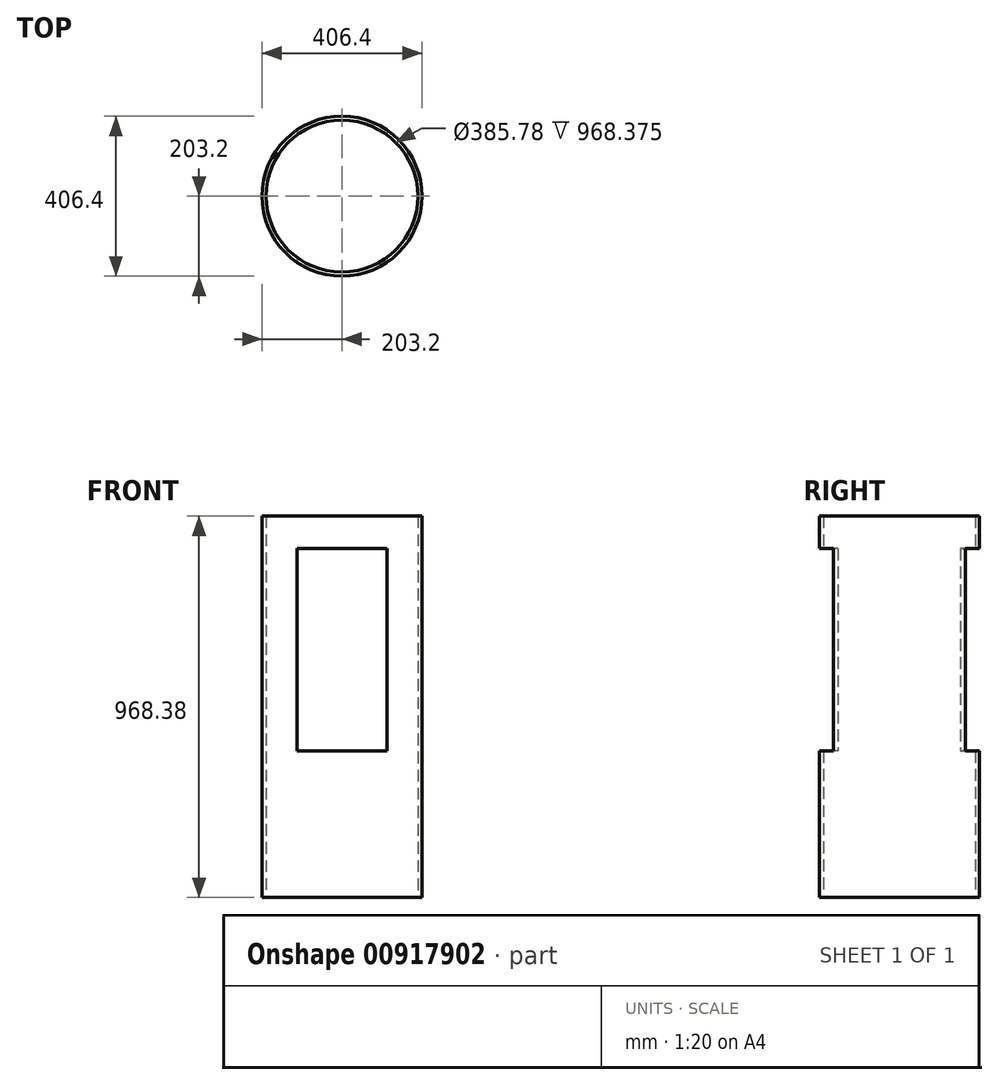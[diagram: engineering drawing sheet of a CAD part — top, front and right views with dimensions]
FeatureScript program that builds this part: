
annotation { "Feature Type Name" : "Feature", "Feature Type Description" : "" }
export const myFeature = defineFeature(function(context is Context, id is Id, definition is map)
    precondition{}
    {
        {
            var Q0;
            Q0=qCreatedBy(makeId("Top.planeOp"),FACE);
            var sketch = newSketch(context, id + "F0", { "sketchPlane" : qUnion([Q0])});
            skCircle(sketch, "E0", {"center": v(0, 0) * mm, "radius": 203.2 * mm});
            skCircle(sketch, "E1", {"center": v(0, 0) * mm, "radius": 192.89 * mm});
            skSolve(sketch);
        }
        {
            var Q0;
            Q0 = qSketchRegion(id + "F0", true);
            extrude(context, id + "F1", {"entities" : qUnion([Q0]), "depth" : 968.38 * mm, "offsetDistance" : 25.4 * mm});
        }
        {
            var Q0;
            Q0=qCreatedBy(makeId("Front.planeOp"),FACE);
            var sketch = newSketch(context, id + "F2", { "sketchPlane" : qUnion([Q0])});
            skLineSegment(sketch, "E2.bottom", {"start": v(114.3, 886.43) * mm, "end": v(-114.3, 886.43) * mm});
            skLineSegment(sketch, "E2.top", {"start": v(114.3, 372.13) * mm, "end": v(-114.3, 372.13) * mm});
            skLineSegment(sketch, "E2.left", {"start": v(114.3, 886.43) * mm, "end": v(114.3, 372.13) * mm});
            skLineSegment(sketch, "E2.right", {"start": v(-114.3, 886.43) * mm, "end": v(-114.3, 372.13) * mm});
            skPoint(sketch, "E2.middle", {"position": v(0, 629.28) * mm});
            skSolve(sketch);
        }
        {
            var Q0;
            Q0 = qSketchRegion(id + "F2", true);
            extrude(context, id + "F3", {"entities" : qUnion([Q0]), "operationType" : NewBodyOperationType.REMOVE, "oppositeDirection" : true, "depth" : 431.8 * mm, "offsetDistance" : 25.4 * mm, "symmetric" : true});
        }
    });
